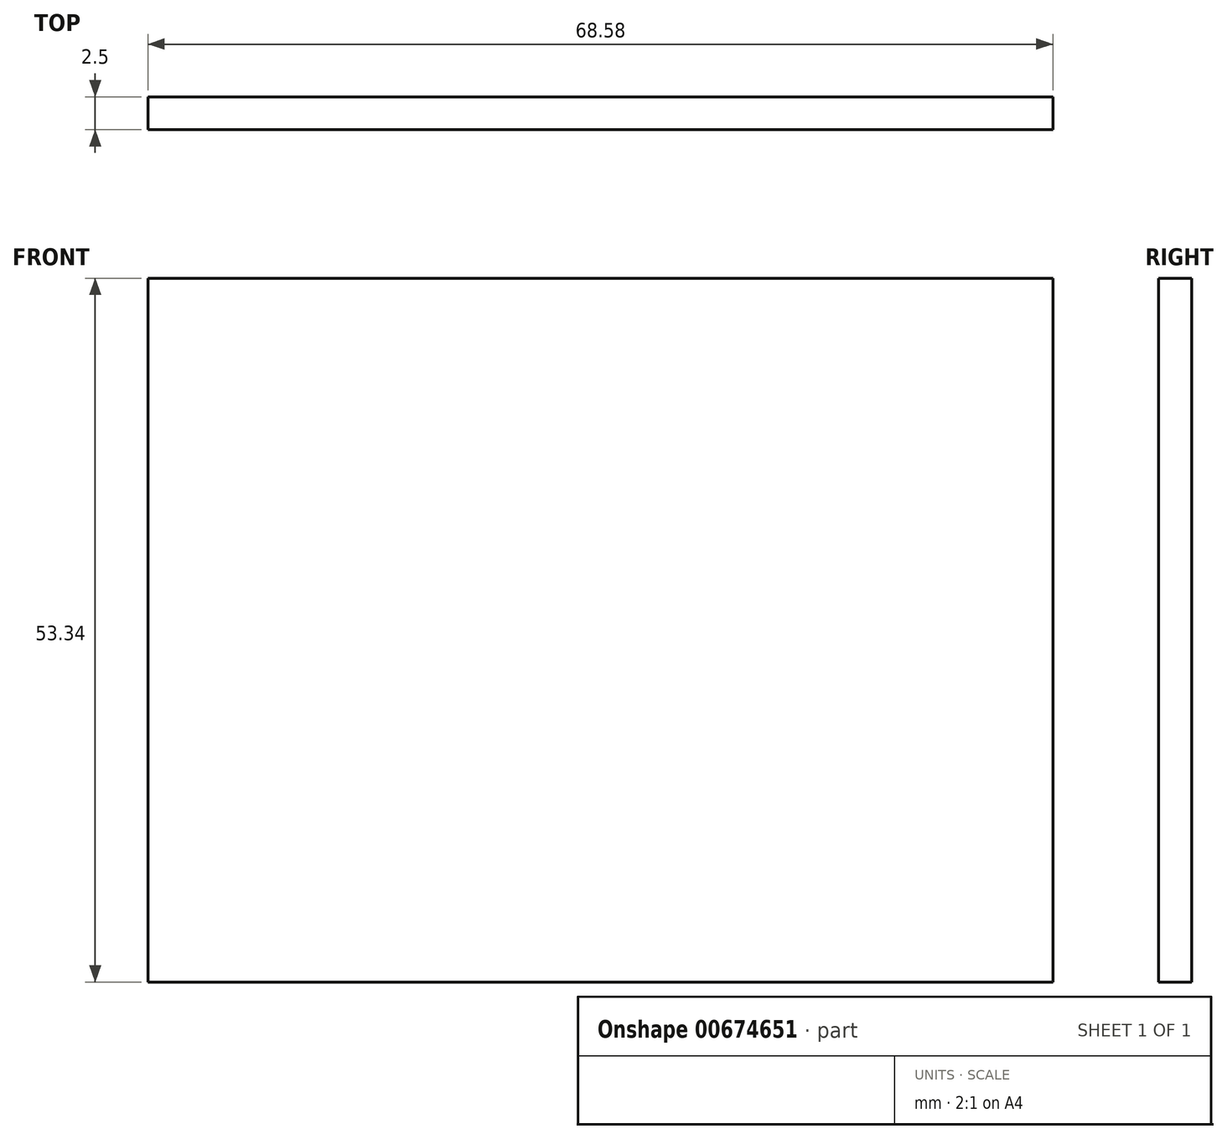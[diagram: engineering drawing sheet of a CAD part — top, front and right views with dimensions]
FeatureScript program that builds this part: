
annotation { "Feature Type Name" : "Feature", "Feature Type Description" : "" }
export const myFeature = defineFeature(function(context is Context, id is Id, definition is map)
    precondition{}
    {
        {
            var Q0;
            Q0=qCreatedBy(makeId("Front.planeOp"),FACE);
            var sketch = newSketch(context, id + "F0", { "sketchPlane" : qUnion([Q0])});
            skLineSegment(sketch, "E0.bottom", {"start": v(0, 0) * mm, "end": v(68.58, 0) * mm});
            skLineSegment(sketch, "E0.top", {"start": v(0, 53.34) * mm, "end": v(68.58, 53.34) * mm});
            skLineSegment(sketch, "E0.left", {"start": v(0, 0) * mm, "end": v(0, 53.34) * mm});
            skLineSegment(sketch, "E0.right", {"start": v(68.58, 0) * mm, "end": v(68.58, 53.34) * mm});
            skSolve(sketch);
        }
        {
            var Q0;
            Q0=makeQuery(id+"F0.imprint","IMPRINT",FACE,{"disambiguationData":[TD([[makeQuery(id+"F0.imprint","IMPRINT",EDGE,{"derivedFrom":sQuery(id+"F0.wireOp",EDGE,"E0.bottom")}),1.0]])]});
            extrude(context, id + "F1", {"entities" : qUnion([Q0]), "depth" : 2.5 * mm, "offsetDistance" : 25.4 * mm});
        }
    });
